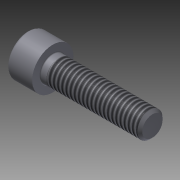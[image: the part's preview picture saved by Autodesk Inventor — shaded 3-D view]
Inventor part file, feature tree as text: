
AUTODESK INVENTOR PART (.ipt)
format: ipt  version: 2014 (Build 180170000, 170)  size: 170,496 bytes
history: native  units: mm (DEFAULTED — no unit token found)
features: sketch x2, extrude x1, plane x1, fillet x1
ambient origin geometry x7: Origin, YZ Plane, XY Plane, X Axis, Y Axis, Z Axis, Center Point
bodies: Solid1 (feature_tree), Body (feature_tree)
feature tree (5):
  extrude  "Slot"  Depth=4.826mm
  plane  "Work Plane1"
  fillet  "Fillet2"  Radius=4.826mm
  sketch  "Sketch1"  dims[d1=17.859048mm d2=1.190852mm d3=4.826mm]
  sketch  "Sketch2"  dims[d4=2.286mm d5=60.0deg d6=4.826mm d7=4.826mm d8=4.575385mm d9=7.9248mm d10=90.0deg d11=10.0mm d12=0.0mm d13=17.859048mm d14=0.0mm d15=0.47244mm d16=0.47244mm d17=0.4572mm d19=0.0mm d26=19.05mm d27=45.0deg d28=0.0mm d29=0.0mm d30=0.1524mm]
